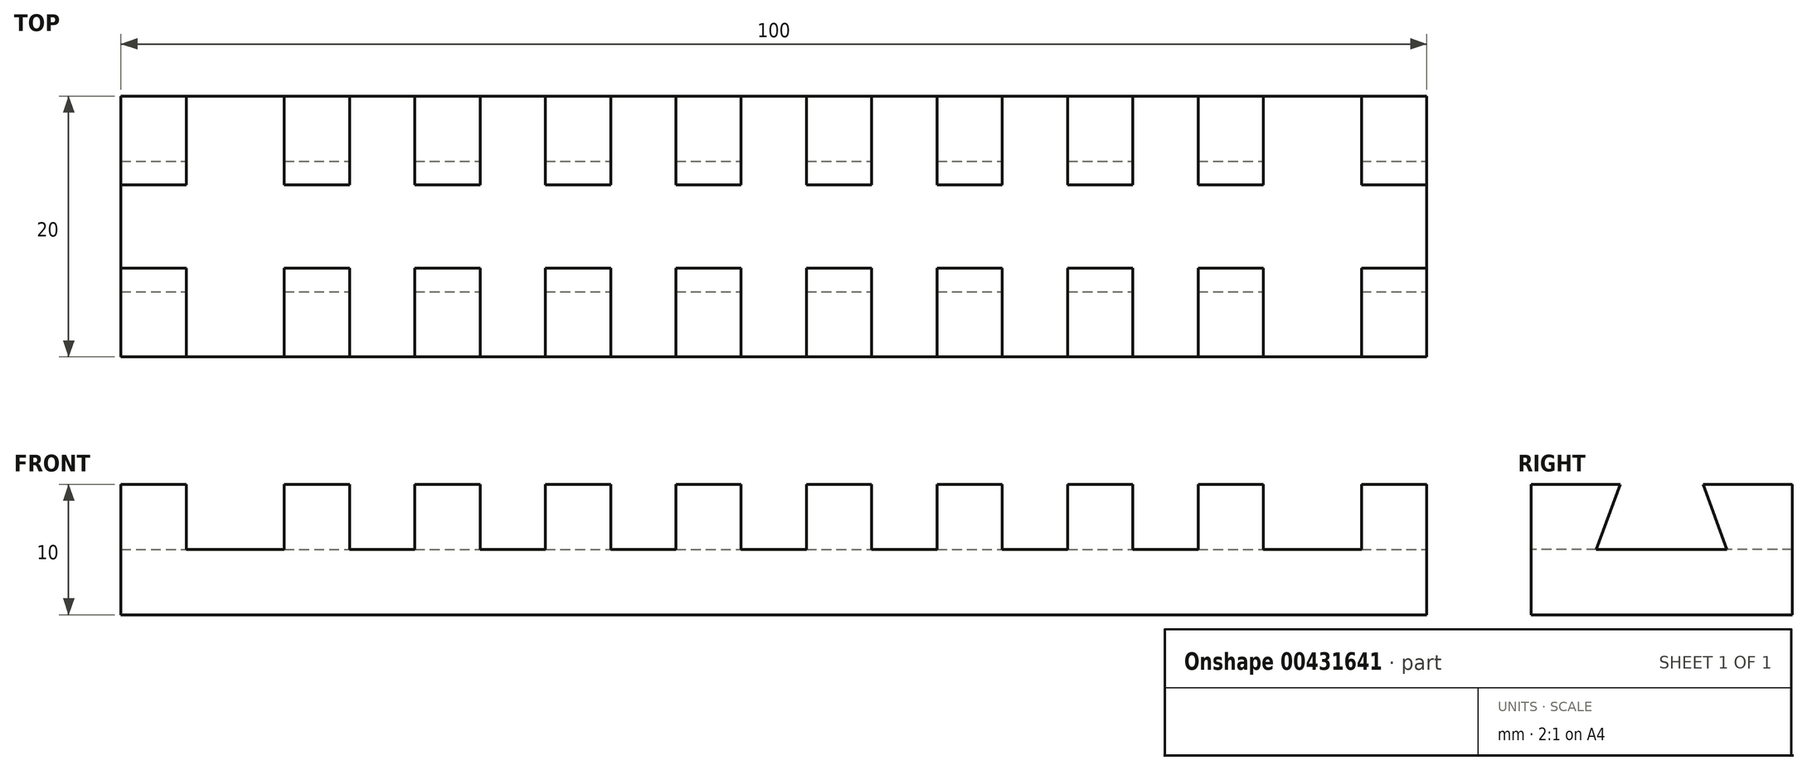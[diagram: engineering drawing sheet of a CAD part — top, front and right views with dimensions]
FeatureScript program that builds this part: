
annotation { "Feature Type Name" : "Feature", "Feature Type Description" : "" }
export const myFeature = defineFeature(function(context is Context, id is Id, definition is map)
    precondition{}
    {
        {
            var Q0;
            Q0=qCreatedBy(makeId("Top.planeOp"),FACE);
            var sketch = newSketch(context, id + "F0", { "sketchPlane" : qUnion([Q0])});
            skLineSegment(sketch, "E0.bottom", {"start": v(-50, 10) * mm, "end": v(50, 10) * mm});
            skLineSegment(sketch, "E0.top", {"start": v(-50, -10) * mm, "end": v(50, -10) * mm});
            skLineSegment(sketch, "E0.left", {"start": v(-50, 10) * mm, "end": v(-50, -10) * mm});
            skLineSegment(sketch, "E0.right", {"start": v(50, 10) * mm, "end": v(50, -10) * mm});
            skSolve(sketch);
        }
        {
            var Q0;
            Q0=makeQuery(id+"F0.imprint","IMPRINT",FACE,{"disambiguationData":[TD([[makeQuery(id+"F0.imprint","IMPRINT",EDGE,{"derivedFrom":sQuery(id+"F0.wireOp",EDGE,"E0.bottom")}),-1.0]])]});
            extrude(context, id + "F1", {"entities" : qUnion([Q0]), "depth" : 10 * mm});
        }
        {
            var Q0;
            Q0=makeQuery(id+"F1.opExtrude","SWEPT_FACE",FACE,{"disambiguationData":[OSD([sQuery(id+"F0.wireOp",EDGE,"E0.right")])]});
            var sketch = newSketch(context, id + "F2", { "sketchPlane" : qUnion([Q0])});
            skLineSegment(sketch, "E1", {"start": v(-3.18, 10) * mm, "end": v(-5, 5) * mm});
            skLineSegment(sketch, "E2", {"start": v(-5, 5) * mm, "end": v(5, 5) * mm});
            skLineSegment(sketch, "E3", {"start": v(5, 5) * mm, "end": v(3.18, 10) * mm});
            skLineSegment(sketch, "E4", {"start": v(3.18, 10) * mm, "end": v(-3.18, 10) * mm});
            skLineSegment(sketch, "E5", {"start": v(-5, 5) * mm, "end": v(-10, 5) * mm, "construction": true});
            skPoint(sketch, "E5.endSnap0", {"position": v(-10, 5) * mm});
            skLineSegment(sketch, "E6", {"start": v(10, 5) * mm, "end": v(5, 5) * mm, "construction": true});
            skSolve(sketch);
        }
        {
            var Q0;
            Q0=makeQuery(id+"F2.imprint","IMPRINT",FACE,{"disambiguationData":[TD([[makeQuery(id+"F2.imprint","IMPRINT",EDGE,{"derivedFrom":sQuery(id+"F2.wireOp",EDGE,"E1")}),1.0]])]});
            extrude(context, id + "F3", {"entities" : qUnion([Q0]), "operationType" : NewBodyOperationType.REMOVE, "endBound" : BoundingType.THROUGH_ALL, "oppositeDirection" : true, "depth" : 25 * mm});
        }
        {
            var Q0;
            Q0=makeQuery(id+"F1.opExtrude","SWEPT_FACE",FACE,{"disambiguationData":[OSD([sQuery(id+"F0.wireOp",EDGE,"E0.top")])]});
            var sketch = newSketch(context, id + "F4", { "sketchPlane" : qUnion([Q0])});
            skLineSegment(sketch, "E7.bottom", {"start": v(-45, 10) * mm, "end": v(-37.5, 10) * mm});
            skLineSegment(sketch, "E7.top", {"start": v(-45, 5) * mm, "end": v(-37.5, 5) * mm});
            skLineSegment(sketch, "E7.left", {"start": v(-45, 10) * mm, "end": v(-45, 5) * mm});
            skLineSegment(sketch, "E7.right", {"start": v(-37.5, 10) * mm, "end": v(-37.5, 5) * mm});
            skPoint(sketch, "E8", {"position": v(-50, 5) * mm});
            skLineSegment(sketch, "E9.bottom", {"start": v(-32.5, 10) * mm, "end": v(-27.5, 10) * mm});
            skLineSegment(sketch, "E9.top", {"start": v(-32.5, 5) * mm, "end": v(-27.5, 5) * mm});
            skLineSegment(sketch, "E9.left", {"start": v(-32.5, 10) * mm, "end": v(-32.5, 5) * mm});
            skLineSegment(sketch, "E9.right", {"start": v(-27.5, 10) * mm, "end": v(-27.5, 5) * mm});
            skLineSegment(sketch, "E10.1.0.0", {"start": v(-17.5, 10) * mm, "end": v(-17.5, 5) * mm});
            skLineSegment(sketch, "E10.1.0.1", {"start": v(-22.5, 10) * mm, "end": v(-17.5, 10) * mm});
            skLineSegment(sketch, "E10.1.0.2", {"start": v(-22.5, 10) * mm, "end": v(-22.5, 5) * mm});
            skLineSegment(sketch, "E10.1.0.3", {"start": v(-22.5, 5) * mm, "end": v(-17.5, 5) * mm});
            skLineSegment(sketch, "E10.2.0.0", {"start": v(-7.5, 10) * mm, "end": v(-7.5, 5) * mm});
            skLineSegment(sketch, "E10.2.0.1", {"start": v(-12.5, 10) * mm, "end": v(-7.5, 10) * mm});
            skLineSegment(sketch, "E10.2.0.2", {"start": v(-12.5, 10) * mm, "end": v(-12.5, 5) * mm});
            skLineSegment(sketch, "E10.2.0.3", {"start": v(-12.5, 5) * mm, "end": v(-7.5, 5) * mm});
            skLineSegment(sketch, "E10.3.0.0", {"start": v(2.5, 10) * mm, "end": v(2.5, 5) * mm});
            skLineSegment(sketch, "E10.3.0.1", {"start": v(-2.5, 10) * mm, "end": v(2.5, 10) * mm});
            skLineSegment(sketch, "E10.3.0.2", {"start": v(-2.5, 10) * mm, "end": v(-2.5, 5) * mm});
            skLineSegment(sketch, "E10.3.0.3", {"start": v(-2.5, 5) * mm, "end": v(2.5, 5) * mm});
            skLineSegment(sketch, "E10.4.0.0", {"start": v(12.5, 10) * mm, "end": v(12.5, 5) * mm});
            skLineSegment(sketch, "E10.4.0.1", {"start": v(7.5, 10) * mm, "end": v(12.5, 10) * mm});
            skLineSegment(sketch, "E10.4.0.2", {"start": v(7.5, 10) * mm, "end": v(7.5, 5) * mm});
            skLineSegment(sketch, "E10.4.0.3", {"start": v(7.5, 5) * mm, "end": v(12.5, 5) * mm});
            skLineSegment(sketch, "E10.5.0.0", {"start": v(22.5, 10) * mm, "end": v(22.5, 5) * mm});
            skLineSegment(sketch, "E10.5.0.1", {"start": v(17.5, 10) * mm, "end": v(22.5, 10) * mm});
            skLineSegment(sketch, "E10.5.0.2", {"start": v(17.5, 10) * mm, "end": v(17.5, 5) * mm});
            skLineSegment(sketch, "E10.5.0.3", {"start": v(17.5, 5) * mm, "end": v(22.5, 5) * mm});
            skLineSegment(sketch, "E10.6.0.0", {"start": v(32.5, 10) * mm, "end": v(32.5, 5) * mm});
            skLineSegment(sketch, "E10.6.0.1", {"start": v(27.5, 10) * mm, "end": v(32.5, 10) * mm});
            skLineSegment(sketch, "E10.6.0.2", {"start": v(27.5, 10) * mm, "end": v(27.5, 5) * mm});
            skLineSegment(sketch, "E10.6.0.3", {"start": v(27.5, 5) * mm, "end": v(32.5, 5) * mm});
            skLineSegment(sketch, "E10.direction1", {"start": v(-32.5, 5) * mm, "end": v(-22.5, 5) * mm, "construction": true});
            skLineSegment(sketch, "E11.MirrorCS", {"start": v(37.5, 10) * mm, "end": v(37.5, 5) * mm});
            skLineSegment(sketch, "E12.MirrorCS", {"start": v(45, 10) * mm, "end": v(45, 5) * mm});
            skLineSegment(sketch, "E13.MirrorCS", {"start": v(45, 10) * mm, "end": v(37.5, 10) * mm});
            skLineSegment(sketch, "E14.MirrorCS", {"start": v(45, 5) * mm, "end": v(37.5, 5) * mm});
            skSolve(sketch);
        }
        {
            var Q0;
            Q0 = qSketchRegion(id + "F4", true);
            extrude(context, id + "F5", {"entities" : qUnion([Q0]), "operationType" : NewBodyOperationType.REMOVE, "endBound" : BoundingType.THROUGH_ALL, "oppositeDirection" : true, "depth" : 25 * mm});
        }
    });
